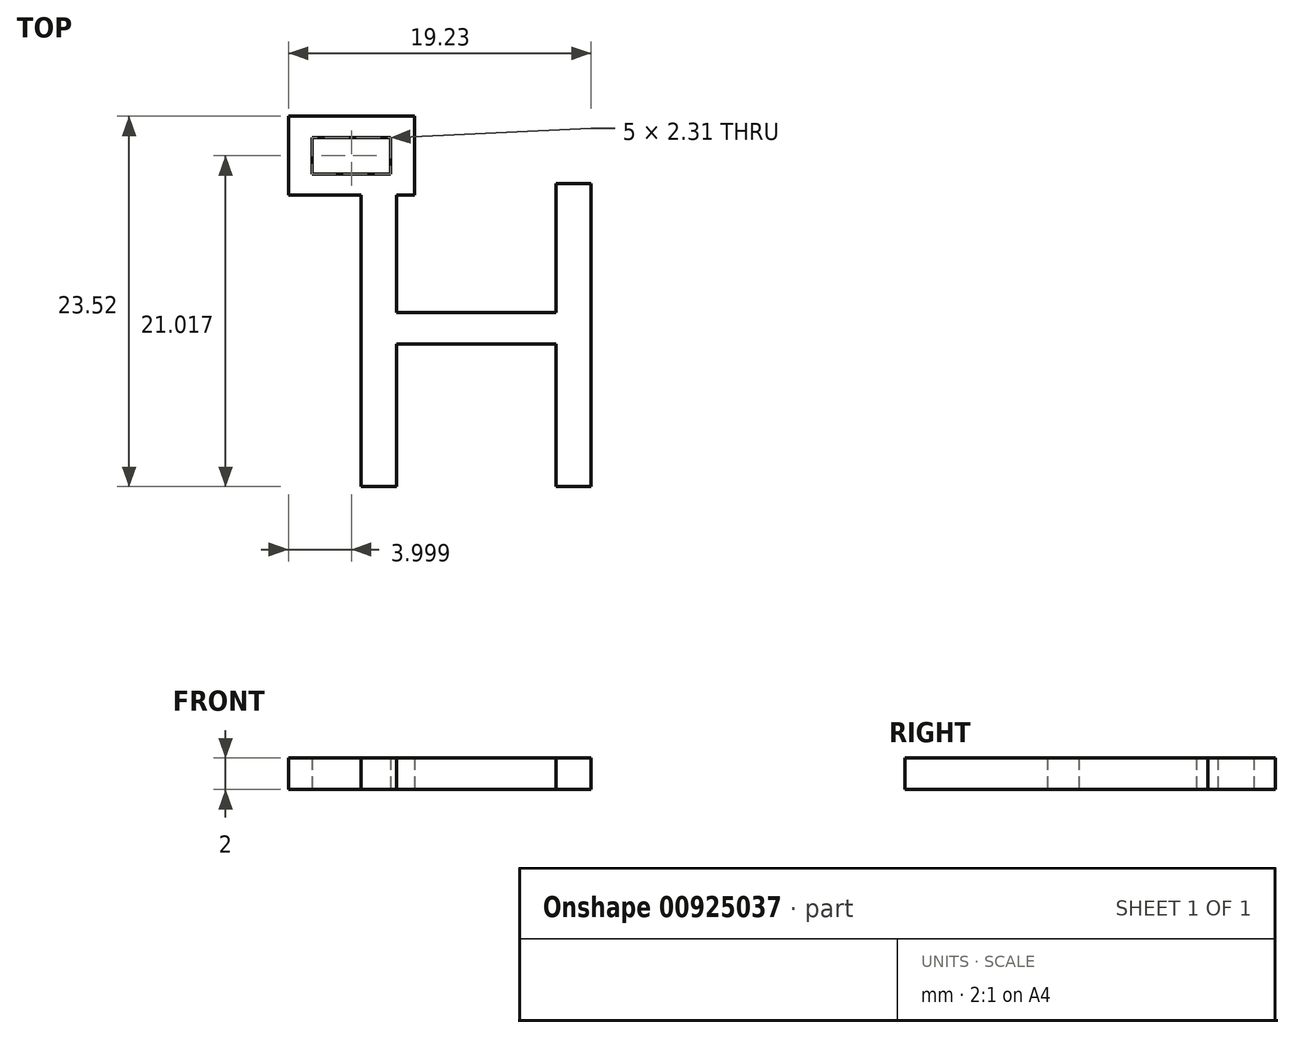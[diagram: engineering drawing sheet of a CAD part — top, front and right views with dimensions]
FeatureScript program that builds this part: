
annotation { "Feature Type Name" : "Feature", "Feature Type Description" : "" }
export const myFeature = defineFeature(function(context is Context, id is Id, definition is map)
    precondition{}
    {
        {
            var Q0;
            Q0=qCreatedBy(makeId("Top.planeOp"),FACE);
            var sketch = newSketch(context, id + "F0", { "sketchPlane" : qUnion([Q0])});
            skText(sketch, "E0", { "text": "H", "fontName": "OpenSans-Regular.ttf"});
            skLineSegment(sketch, "E1.bottom", {"start": v(6.02, -0.88) * mm, "end": v(-1.98, -0.88) * mm});
            skLineSegment(sketch, "E1.top", {"start": v(6.02, 4.12) * mm, "end": v(-1.98, 4.12) * mm});
            skLineSegment(sketch, "E1.left", {"start": v(6.02, -0.88) * mm, "end": v(6.02, 4.12) * mm});
            skLineSegment(sketch, "E1.right", {"start": v(-1.98, -0.88) * mm, "end": v(-1.98, 4.12) * mm});
            skLineSegment(sketch, "E2", {"start": v(2.02, 4.12) * mm, "end": v(2.02, -0.88) * mm});
            skLineSegment(sketch, "E3.bottom", {"start": v(4.52, 0.46) * mm, "end": v(-0.48, 0.46) * mm});
            skLineSegment(sketch, "E3.top", {"start": v(4.52, 2.77) * mm, "end": v(-0.48, 2.77) * mm});
            skLineSegment(sketch, "E3.left", {"start": v(4.52, 0.46) * mm, "end": v(4.52, 2.77) * mm});
            skLineSegment(sketch, "E3.right", {"start": v(-0.48, 0.46) * mm, "end": v(-0.48, 2.77) * mm});
            skPoint(sketch, "E3.middle", {"position": v(2.02, 1.62) * mm});
            const initialGuessF0  = {"E0": [0, -0.0194, 1, 0, 0.0194]};
            skSetInitialGuess(sketch, initialGuessF0);
            skSolve(sketch);
        }
        {
            var Q0;
            Q0 = qSketchRegion(id + "F0", true);
            extrude(context, id + "F1", {"entities" : qUnion([Q0]), "depth" : 2 * mm, "offsetDistance" : 25 * mm});
        }
    });
